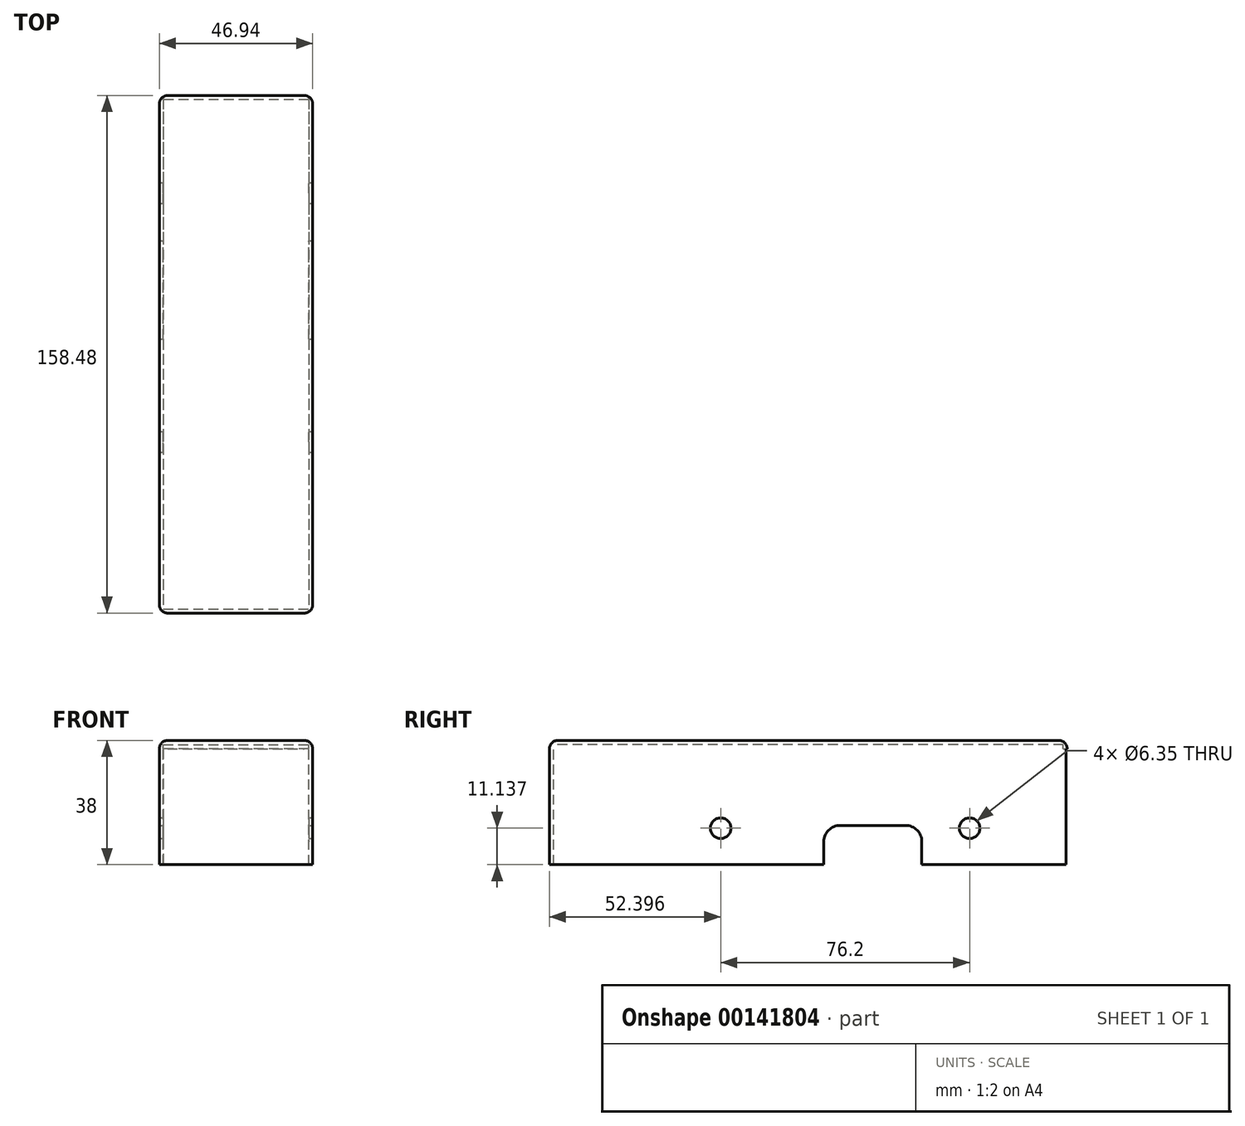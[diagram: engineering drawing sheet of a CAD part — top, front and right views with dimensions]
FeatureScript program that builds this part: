
annotation { "Feature Type Name" : "Feature", "Feature Type Description" : "" }
export const myFeature = defineFeature(function(context is Context, id is Id, definition is map)
    precondition{}
    {
        {
            var Q0;
            Q0=qCreatedBy(makeId("Top.planeOp"),FACE);
            var sketch = newSketch(context, id + "F0", { "sketchPlane" : qUnion([Q0])});
            skLineSegment(sketch, "E0.bottom", {"start": v(-23.47, 79.24) * mm, "end": v(23.47, 79.24) * mm});
            skLineSegment(sketch, "E0.top", {"start": v(-23.47, -79.24) * mm, "end": v(23.47, -79.24) * mm});
            skLineSegment(sketch, "E0.left", {"start": v(-23.47, 79.24) * mm, "end": v(-23.47, -79.24) * mm});
            skLineSegment(sketch, "E0.right", {"start": v(23.47, 79.24) * mm, "end": v(23.47, -79.24) * mm});
            skPoint(sketch, "E0.middle", {"position": v(0, 0) * mm});
            skSolve(sketch);
        }
        {
            var Q0;
            Q0 = qSketchRegion(id + "F0", true);
            extrude(context, id + "F1", {"entities" : qUnion([Q0]), "oppositeDirection" : true, "depth" : 38 * mm});
        }
        {
            var Q0;
            Q0=makeQuery(id+"F1.opExtrude","CAP_FACE",FACE,{"disambiguationData":[OSD([sQuery(id+"F0.wireOp",EDGE,"E0.bottom"),sQuery(id+"F0.wireOp",EDGE,"E0.top"),sQuery(id+"F0.wireOp",EDGE,"E0.left"),sQuery(id+"F0.wireOp",EDGE,"E0.right")])],"isStart":false});
            shell(context, id + "F2", {"entities" : qUnion([Q0]), "thickness" : 1.22 * mm});
        }
        {
            var Q0;
            Q0=makeQuery(id+"F1.opExtrude","CAP_EDGE",EDGE,{"disambiguationData":[OSD([sQuery(id+"F0.wireOp",EDGE,"E0.right")])],"isStart":true});
            var Q1;
            Q1=makeQuery(id+"F1.opExtrude","CAP_EDGE",EDGE,{"disambiguationData":[OSD([sQuery(id+"F0.wireOp",EDGE,"E0.left")])],"isStart":true});
            var Q2;
            Q2=makeQuery(id+"F1.opExtrude","CAP_EDGE",EDGE,{"disambiguationData":[OSD([sQuery(id+"F0.wireOp",EDGE,"E0.top")])],"isStart":true});
            var Q3;
            Q3=makeQuery(id+"F1.opExtrude","SWEPT_EDGE",EDGE,{"disambiguationData":[OSD([sQuery(id+"F0.wireOp",EDGE,"E0.top"),sQuery(id+"F0.wireOp",EDGE,"E0.right")])]});
            var Q4;
            Q4=makeQuery(id+"F1.opExtrude","SWEPT_EDGE",EDGE,{"disambiguationData":[OSD([sQuery(id+"F0.wireOp",EDGE,"E0.top"),sQuery(id+"F0.wireOp",EDGE,"E0.left")])]});
            var Q5;
            Q5=makeQuery(id+"F1.opExtrude","SWEPT_EDGE",EDGE,{"disambiguationData":[OSD([sQuery(id+"F0.wireOp",EDGE,"E0.bottom"),sQuery(id+"F0.wireOp",EDGE,"E0.left")])]});
            var Q6;
            Q6=makeQuery(id+"F1.opExtrude","SWEPT_EDGE",EDGE,{"disambiguationData":[OSD([sQuery(id+"F0.wireOp",EDGE,"E0.bottom"),sQuery(id+"F0.wireOp",EDGE,"E0.right")])]});
            var Q7;
            Q7=makeQuery(id+"F1.opExtrude","CAP_EDGE",EDGE,{"disambiguationData":[OSD([sQuery(id+"F0.wireOp",EDGE,"E0.bottom")])],"isStart":true});
            fillet(context, id + "F3", {"entities" : qUnion([Q0, Q1, Q2, Q3, Q4, Q5, Q6, Q7]), "radius" : 2.54 * mm, "tangentPropagation" : true, "allowEdgeOverflow" : false});
        }
        {
            var Q0;
            Q0=makeQuery(id+"F1.opExtrude","SWEPT_FACE",FACE,{"disambiguationData":[OSD([sQuery(id+"F0.wireOp",EDGE,"E0.right")])]});
            var sketch = newSketch(context, id + "F4", { "sketchPlane" : qUnion([Q0])});
            skLineSegment(sketch, "E1.0", {"start": v(79.24, -2.54) * mm, "end": v(79.24, -38) * mm});
            skLineSegment(sketch, "E1.1", {"start": v(34.74, -38) * mm, "end": v(4.74, -38) * mm});
            skLineSegment(sketch, "E2.0", {"start": v(34.74, -31) * mm, "end": v(34.74, -38) * mm});
            skLineSegment(sketch, "E3.0", {"start": v(29.74, -26) * mm, "end": v(9.74, -26) * mm});
            skLineSegment(sketch, "E4.0", {"start": v(4.74, -31) * mm, "end": v(4.74, -38) * mm});
            skPoint(sketch, "E5.orphan", {"position": v(-76.7, -38) * mm});
            skPoint(sketch, "E6.orphan", {"position": v(76.7, -38) * mm});
            skArc(sketch, "E7", {"start": v(9.74, -26) * mm, "mid": v(6.2, -27.47) * mm, "end": v(4.74, -31) * mm});
            skArc(sketch, "E8", {"start": v(34.74, -31) * mm, "mid": v(33.28, -27.47) * mm, "end": v(29.74, -26) * mm});
            skSolve(sketch);
        }
        {
            var Q0;
            Q0 = qSketchRegion(id + "F4", true);
            extrude(context, id + "F5", {"entities" : qUnion([Q0]), "operationType" : NewBodyOperationType.REMOVE, "endBound" : BoundingType.THROUGH_ALL, "oppositeDirection" : true, "depth" : 25.4 * mm});
        }
        {
            var Q0;
            Q0=makeQuery(id+"F1.opExtrude","SWEPT_FACE",FACE,{"disambiguationData":[OSD([sQuery(id+"F0.wireOp",EDGE,"E0.right")])]});
            var sketch = newSketch(context, id + "F6", { "sketchPlane" : qUnion([Q0])});
            skLineSegment(sketch, "E9.0", {"start": v(4.74, -38) * mm, "end": v(-76.7, -38) * mm});
            skLineSegment(sketch, "E9.1", {"start": v(-79.24, -38) * mm, "end": v(-79.24, -2.54) * mm});
            skCircle(sketch, "E10", {"center": v(-26.84, -26.86) * mm, "radius": 3.18 * mm});
            skCircle(sketch, "E11", {"center": v(49.36, -26.86) * mm, "radius": 3.18 * mm});
            skSolve(sketch);
        }
        {
            var Q0;
            Q0 = qSketchRegion(id + "F6", true);
            extrude(context, id + "F7", {"entities" : qUnion([Q0]), "operationType" : NewBodyOperationType.REMOVE, "endBound" : BoundingType.THROUGH_ALL, "oppositeDirection" : true, "depth" : 25.4 * mm});
        }
        {
            var Q0;
            Q0=makeQuery(id+"F1.opExtrude","SWEPT_FACE",FACE,{"disambiguationData":[OSD([sQuery(id+"F0.wireOp",EDGE,"E0.bottom")])]});
            var sketch = newSketch(context, id + "F8", { "sketchPlane" : qUnion([Q0])});
            skLineSegment(sketch, "E12.0", {"start": v(-23.47, -38) * mm, "end": v(-23.47, -2.54) * mm});
            skLineSegment(sketch, "E12.1", {"start": v(23.47, -2.54) * mm, "end": v(23.47, -38) * mm});
            skLineSegment(sketch, "E13.0", {"start": v(22.25, -2.54) * mm, "end": v(22.25, -38) * mm});
            skLineSegment(sketch, "E14.0", {"start": v(-22.25, -38) * mm, "end": v(-22.25, -2.54) * mm});
            skLineSegment(sketch, "E15", {"start": v(-22.25, -2.54) * mm, "end": v(22.25, -2.54) * mm});
            skLineSegment(sketch, "E16", {"start": v(22.25, -38) * mm, "end": v(-22.25, -38) * mm});
            skSolve(sketch);
        }
        {
            var Q0;
            Q0 = qSketchRegion(id + "F8", true);
            extrude(context, id + "F9", {"entities" : qUnion([Q0]), "operationType" : NewBodyOperationType.REMOVE, "endBound" : BoundingType.UP_TO_NEXT, "oppositeDirection" : true, "depth" : 25.4 * mm});
        }
    });
